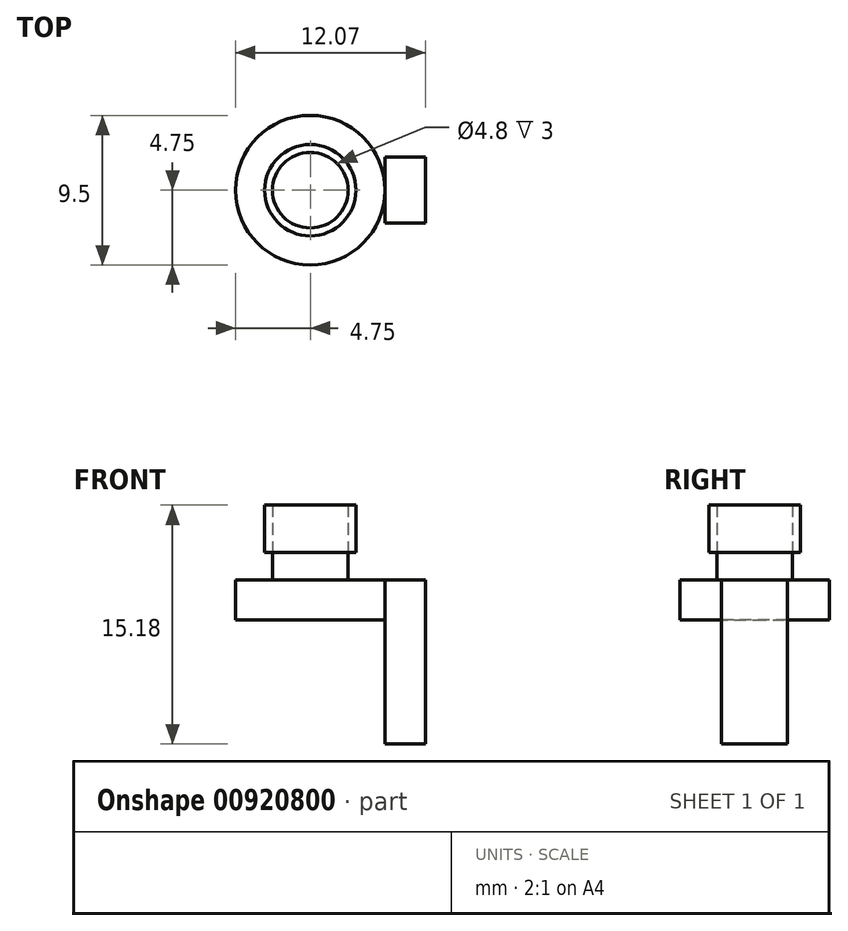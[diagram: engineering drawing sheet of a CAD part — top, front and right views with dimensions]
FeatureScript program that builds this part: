
annotation { "Feature Type Name" : "Feature", "Feature Type Description" : "" }
export const myFeature = defineFeature(function(context is Context, id is Id, definition is map)
    precondition{}
    {
        {
            var Q0;
            Q0=qCreatedBy(makeId("Top.planeOp"),FACE);
            var sketch = newSketch(context, id + "F0", { "sketchPlane" : qUnion([Q0])});
            skCircle(sketch, "E0", {"center": v(0, 0) * mm, "radius": 2.4 * mm});
            skSolve(sketch);
        }
        {
            var Q0;
            Q0=makeQuery(id+"F0.imprint","IMPRINT",FACE,{"disambiguationData":[TD([[makeQuery(id+"F0.imprint","IMPRINT",EDGE,{"derivedFrom":sQuery(id+"F0.wireOp",EDGE,"E0")}),1.0]])]});
            extrude(context, id + "F1", {"entities" : qUnion([Q0]), "depth" : 1.74 * mm, "offsetDistance" : 25 * mm});
        }
        {
            var Q0;
            Q0=makeQuery(id+"F1.opExtrude","CAP_FACE",FACE,{"disambiguationData":[OSD([sQuery(id+"F0.wireOp",EDGE,"E0")])],"isStart":false});
            var sketch = newSketch(context, id + "F2", { "sketchPlane" : qUnion([Q0])});
            skCircle(sketch, "E1", {"center": v(0, 0) * mm, "radius": 2.9 * mm});
            skSolve(sketch);
        }
        {
            var Q0;
            Q0=makeQuery(id+"F2.imprint","IMPRINT",FACE,{"disambiguationData":[TD([[makeQuery(id+"F2.imprint","IMPRINT",EDGE,{"derivedFrom":sQuery(id+"F2.wireOp",EDGE,"E1")}),1.0]])]});
            extrude(context, id + "F3", {"entities" : qUnion([Q0]), "depth" : 3 * mm, "offsetDistance" : 25 * mm});
        }
        {
            var Q0;
            Q0=makeQuery(id+"F1.opExtrude","CAP_FACE",FACE,{"disambiguationData":[OSD([sQuery(id+"F0.wireOp",EDGE,"E0")])],"isStart":true});
            var sketch = newSketch(context, id + "F4", { "sketchPlane" : qUnion([Q0])});
            skCircle(sketch, "E2", {"center": v(0, 0) * mm, "radius": 4.75 * mm});
            skSolve(sketch);
        }
        {
            var Q0;
            Q0=makeQuery(id+"F4.imprint","IMPRINT",FACE,{"disambiguationData":[TD([[makeQuery(id+"F4.imprint","IMPRINT",EDGE,{"derivedFrom":sQuery(id+"F4.wireOp",EDGE,"E2")}),1.0]])]});
            var Q1;
            Q1=makeQuery(id+"F4.imprint","IMPRINT",FACE,{"disambiguationData":[TD([[makeQuery(id+"F4.imprint","IMPRINT",EDGE,{"derivedFrom":makeQuery(id+"F1.opExtrude","CAP_EDGE",EDGE,{"disambiguationData":[OSD([sQuery(id+"F0.wireOp",EDGE,"E0")])],"isStart":true})}),-1.0]])]});
            extrude(context, id + "F5", {"entities" : qUnion([Q0, Q1]), "depth" : 2.55 * mm, "offsetDistance" : 25 * mm});
        }
        {
            var Q0;
            Q0=qCreatedBy(makeId("Right.planeOp"),FACE);
            cPlane(context, id + "F6", {"entities" : qUnion([Q0]), "cplaneType" : CPlaneType.OFFSET, "offset" : 4.75 * mm, "width" : 150 * mm, "height" : 150 * mm});
        }
        {
            var Q0;
            Q0=qCreatedBy(id+"F6.planeOp",FACE);
            var sketch = newSketch(context, id + "F7", { "sketchPlane" : qUnion([Q0])});
            skLineSegment(sketch, "E3", {"start": v(0, 0) * mm, "end": v(0, -2.55) * mm});
            skLineSegment(sketch, "E4", {"start": v(0, 0) * mm, "end": v(-2.1, 0) * mm});
            skLineSegment(sketch, "E5", {"start": v(0, 0) * mm, "end": v(2.1, 0) * mm});
            skLineSegment(sketch, "E6", {"start": v(-2.1, 0) * mm, "end": v(-2.1, -10.44) * mm});
            skLineSegment(sketch, "E7", {"start": v(2.1, 0) * mm, "end": v(2.1, -10.44) * mm});
            skLineSegment(sketch, "E8", {"start": v(-2.1, -10.44) * mm, "end": v(2.1, -10.44) * mm});
            skSolve(sketch);
        }
        {
            var Q0;
            Q0=makeQuery(id+"F7.imprint","IMPRINT",FACE,{"disambiguationData":[TD([[makeQuery(id+"F7.imprint","IMPRINT",EDGE,{"derivedFrom":sQuery(id+"F7.wireOp",EDGE,"E4")}),1.0]])]});
            extrude(context, id + "F8", {"entities" : qUnion([Q0]), "operationType" : NewBodyOperationType.ADD, "depth" : 2.57 * mm, "offsetDistance" : 25 * mm});
        }
    });
